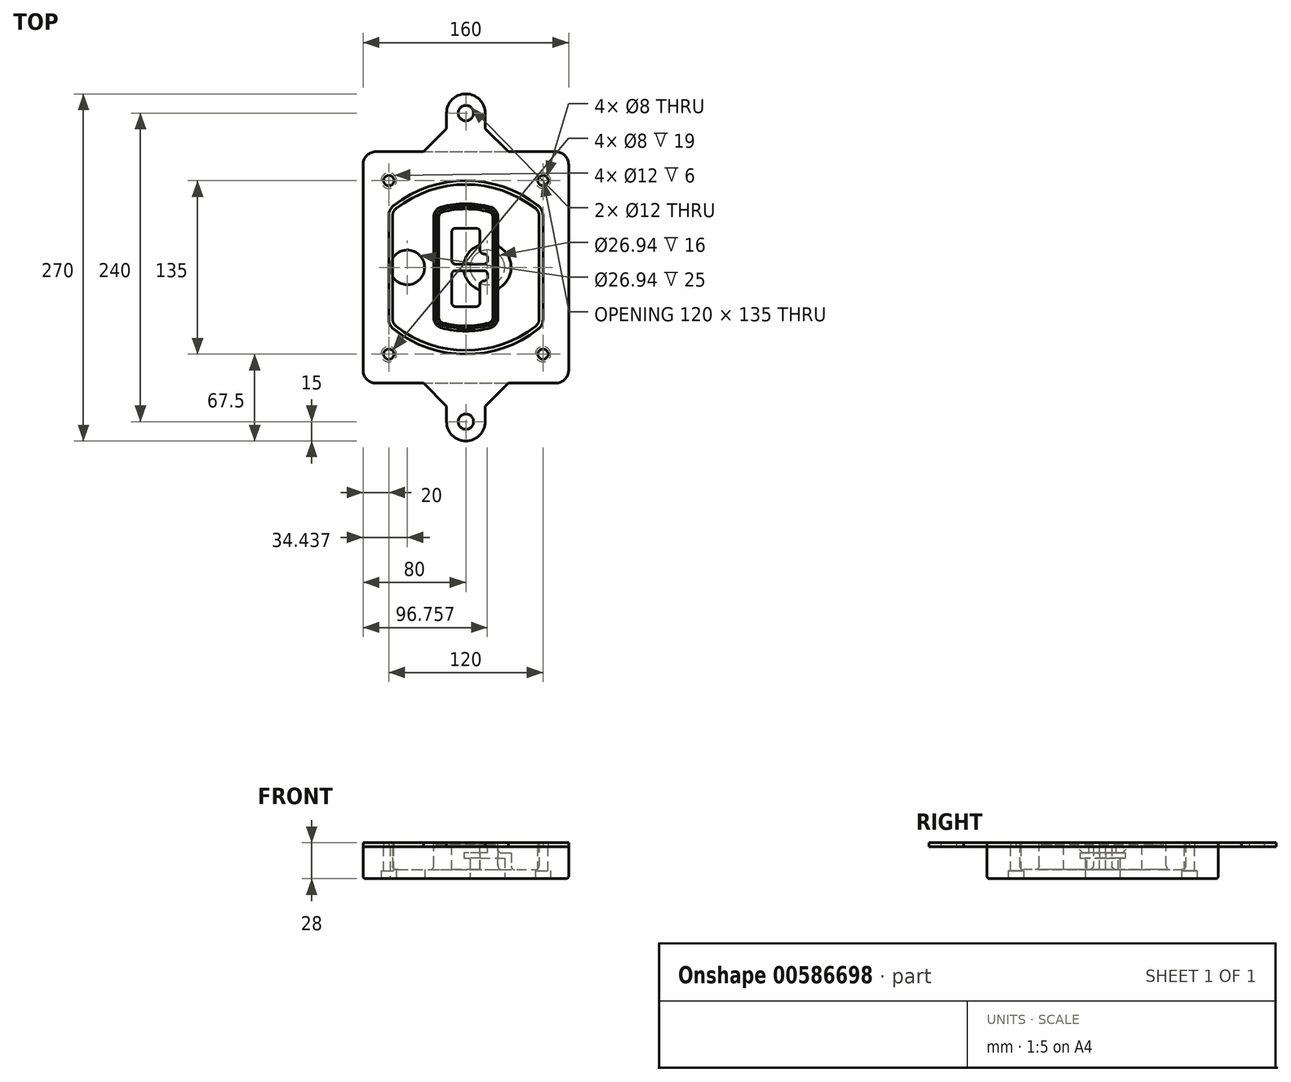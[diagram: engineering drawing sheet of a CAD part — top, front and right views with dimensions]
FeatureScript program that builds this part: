
annotation { "Feature Type Name" : "Feature", "Feature Type Description" : "" }
export const myFeature = defineFeature(function(context is Context, id is Id, definition is map)
    precondition{}
    {
        {
            var Q0;
            Q0=qCreatedBy(makeId("Top.planeOp"),FACE);
            var sketch = newSketch(context, id + "F0", { "sketchPlane" : qUnion([Q0])});
            skPoint(sketch, "E0.rect.middle", {"position": v(0, 0) * mm});
            skLineSegment(sketch, "E1.bottom", {"start": v(-70, -90) * mm, "end": v(70, -90) * mm});
            skLineSegment(sketch, "E1.top", {"start": v(-70, 90) * mm, "end": v(70, 90) * mm});
            skLineSegment(sketch, "E1.left", {"start": v(-80, -80) * mm, "end": v(-80, 80) * mm});
            skLineSegment(sketch, "E1.right", {"start": v(80, -80) * mm, "end": v(80, 80) * mm});
            skLineSegment(sketch, "E2", {"start": v(-80, 90) * mm, "end": v(80, -90) * mm, "construction": true});
            skLineSegment(sketch, "E3", {"start": v(80, 90) * mm, "end": v(-80, -90) * mm, "construction": true});
            skCircle(sketch, "E4", {"center": v(-60, 67.5) * mm, "radius": 4 * mm});
            skCircle(sketch, "E5", {"center": v(60, 67.5) * mm, "radius": 4 * mm});
            skCircle(sketch, "E6", {"center": v(60, -67.5) * mm, "radius": 4 * mm});
            skCircle(sketch, "E7", {"center": v(-60, -67.5) * mm, "radius": 4 * mm});
            skLineSegment(sketch, "E8", {"start": v(-60, 67.5) * mm, "end": v(60, 67.5) * mm, "construction": true});
            skLineSegment(sketch, "E9", {"start": v(60, 67.5) * mm, "end": v(60, -67.5) * mm, "construction": true});
            skLineSegment(sketch, "E10", {"start": v(60, -67.5) * mm, "end": v(-60, -67.5) * mm, "construction": true});
            skLineSegment(sketch, "E11", {"start": v(-60, -67.5) * mm, "end": v(-60, 67.5) * mm, "construction": true});
            skLineSegment(sketch, "E12", {"start": v(-60, 40.3) * mm, "end": v(-60, -40.3) * mm});
            skLineSegment(sketch, "E13", {"start": v(60, 40.3) * mm, "end": v(60, -40.3) * mm});
            skArc(sketch, "E14", {"start": v(56.15, 48.18) * mm, "mid": v(0, 67.5) * mm, "end": v(-56.15, 48.18) * mm});
            skArc(sketch, "E15", {"start": v(-56.15, -48.18) * mm, "mid": v(0, -67.5) * mm, "end": v(56.15, -48.18) * mm});
            skLineSegment(sketch, "E16", {"start": v(-60, 0) * mm, "end": v(60, 0) * mm, "construction": true});
            skPoint(sketch, "E17.visualSharp", {"position": v(-60, -45) * mm});
            skArc(sketch, "E17.filletArc", {"start": v(-60, -40.3) * mm, "mid": v(-58.99, -44.68) * mm, "end": v(-56.15, -48.18) * mm});
            skPoint(sketch, "E18.visualSharp", {"position": v(-60, 45) * mm});
            skArc(sketch, "E18.filletArc", {"start": v(-56.15, 48.18) * mm, "mid": v(-58.99, 44.68) * mm, "end": v(-60, 40.3) * mm});
            skPoint(sketch, "E19.visualSharp", {"position": v(60, 45) * mm});
            skArc(sketch, "E19.filletArc", {"start": v(60, 40.3) * mm, "mid": v(58.99, 44.68) * mm, "end": v(56.15, 48.18) * mm});
            skPoint(sketch, "E20.visualSharp", {"position": v(60, -45) * mm});
            skArc(sketch, "E20.filletArc", {"start": v(56.15, -48.18) * mm, "mid": v(58.99, -44.68) * mm, "end": v(60, -40.3) * mm});
            skPoint(sketch, "E21.visualSharp", {"position": v(-80, 90) * mm});
            skArc(sketch, "E21.filletArc", {"start": v(-70, 90) * mm, "mid": v(-77.07, 87.07) * mm, "end": v(-80, 80) * mm});
            skPoint(sketch, "E22.visualSharp", {"position": v(80, 90) * mm});
            skArc(sketch, "E22.filletArc", {"start": v(80, 80) * mm, "mid": v(77.07, 87.07) * mm, "end": v(70, 90) * mm});
            skPoint(sketch, "E23.visualSharp", {"position": v(80, -90) * mm});
            skArc(sketch, "E23.filletArc", {"start": v(70, -90) * mm, "mid": v(77.07, -87.07) * mm, "end": v(80, -80) * mm});
            skPoint(sketch, "E24.visualSharp", {"position": v(-80, -90) * mm});
            skArc(sketch, "E24.filletArc", {"start": v(-80, -80) * mm, "mid": v(-77.07, -87.07) * mm, "end": v(-70, -90) * mm});
            skArc(sketch, "E25.0", {"start": v(57, 40.3) * mm, "mid": v(56.3, 43.36) * mm, "end": v(54.3, 45.81) * mm});
            skLineSegment(sketch, "E25.1", {"start": v(57, 40.3) * mm, "end": v(57, -40.3) * mm});
            skArc(sketch, "E25.2", {"start": v(54.3, -45.81) * mm, "mid": v(56.3, -43.36) * mm, "end": v(57, -40.3) * mm});
            skArc(sketch, "E25.3", {"start": v(-54.3, -45.81) * mm, "mid": v(0, -64.5) * mm, "end": v(54.3, -45.81) * mm});
            skArc(sketch, "E25.4", {"start": v(-57, -40.3) * mm, "mid": v(-56.3, -43.36) * mm, "end": v(-54.3, -45.81) * mm});
            skArc(sketch, "E25.5", {"start": v(54.3, 45.81) * mm, "mid": v(0, 64.5) * mm, "end": v(-54.3, 45.81) * mm});
            skLineSegment(sketch, "E25.6", {"start": v(-57, 40.3) * mm, "end": v(-57, -40.3) * mm});
            skArc(sketch, "E25.7", {"start": v(-54.3, 45.81) * mm, "mid": v(-56.3, 43.36) * mm, "end": v(-57, 40.3) * mm});
            skArc(sketch, "E26.0", {"start": v(-58.62, 51.33) * mm, "mid": v(-62.58, 46.43) * mm, "end": v(-64, 40.3) * mm});
            skArc(sketch, "E26.1", {"start": v(58.62, 51.33) * mm, "mid": v(0, 71.5) * mm, "end": v(-58.62, 51.33) * mm});
            skArc(sketch, "E26.2", {"start": v(64, 40.3) * mm, "mid": v(62.58, 46.43) * mm, "end": v(58.62, 51.33) * mm});
            skLineSegment(sketch, "E26.3", {"start": v(64, 40.3) * mm, "end": v(64, -40.3) * mm});
            skArc(sketch, "E26.4", {"start": v(58.62, -51.33) * mm, "mid": v(62.58, -46.43) * mm, "end": v(64, -40.3) * mm});
            skLineSegment(sketch, "E26.5", {"start": v(-64, 40.3) * mm, "end": v(-64, -40.3) * mm});
            skArc(sketch, "E26.6", {"start": v(-58.62, -51.33) * mm, "mid": v(0, -71.5) * mm, "end": v(58.62, -51.33) * mm});
            skArc(sketch, "E26.7", {"start": v(-64, -40.3) * mm, "mid": v(-62.58, -46.43) * mm, "end": v(-58.62, -51.33) * mm});
            skSolve(sketch);
        }
        {
            var Q0;
            Q0=makeQuery(id+"F0.imprint","IMPRINT",FACE,{"disambiguationData":[TD([[makeQuery(id+"F0.imprint","IMPRINT",EDGE,{"derivedFrom":sQuery(id+"F0.wireOp",EDGE,"E1.bottom")}),1.0]])]});
            var Q1;
            Q1=makeQuery(id+"F0.imprint","IMPRINT",FACE,{"disambiguationData":[TD([[makeQuery(id+"F0.imprint","IMPRINT",EDGE,{"derivedFrom":sQuery(id+"F0.wireOp",EDGE,"E12")}),1.0]])]});
            var Q2;
            Q2=makeQuery(id+"F0.imprint","IMPRINT",FACE,{"disambiguationData":[TD([[makeQuery(id+"F0.imprint","IMPRINT",EDGE,{"derivedFrom":sQuery(id+"F0.wireOp",EDGE,"E25.0")}),1.0]])]});
            var Q3;
            Q3=makeQuery(id+"F0.imprint","IMPRINT",FACE,{"disambiguationData":[TD([[makeQuery(id+"F0.imprint","IMPRINT",EDGE,{"derivedFrom":sQuery(id+"F0.wireOp",EDGE,"E12")}),-1.0]])]});
            extrude(context, id + "F1", {"entities" : qUnion([Q0, Q1, Q2, Q3]), "oppositeDirection" : true, "depth" : 25 * mm});
        }
        {
            var Q0;
            Q0=makeQuery(id+"F0.imprint","IMPRINT",FACE,{"disambiguationData":[TD([[makeQuery(id+"F0.imprint","IMPRINT",EDGE,{"derivedFrom":sQuery(id+"F0.wireOp",EDGE,"E12")}),1.0]])]});
            extrude(context, id + "F2", {"entities" : qUnion([Q0]), "operationType" : NewBodyOperationType.ADD, "depth" : 3 * mm});
        }
        {
            var Q0;
            Q0=makeQuery(id+"F0.imprint","IMPRINT",FACE,{"disambiguationData":[TD([[makeQuery(id+"F0.imprint","IMPRINT",EDGE,{"derivedFrom":sQuery(id+"F0.wireOp",EDGE,"E25.0")}),1.0]])]});
            extrude(context, id + "F3", {"entities" : qUnion([Q0]), "operationType" : NewBodyOperationType.REMOVE, "oppositeDirection" : true, "depth" : 18 * mm});
        }
        {
            var Q0;
            Q0=makeQuery(id+"F2.opExtrude","CAP_FACE",FACE,{"disambiguationData":[OSD([sQuery(id+"F0.wireOp",EDGE,"E12"),sQuery(id+"F0.wireOp",EDGE,"E13"),sQuery(id+"F0.wireOp",EDGE,"E14"),sQuery(id+"F0.wireOp",EDGE,"E15"),sQuery(id+"F0.wireOp",EDGE,"E17.filletArc"),sQuery(id+"F0.wireOp",EDGE,"E18.filletArc"),sQuery(id+"F0.wireOp",EDGE,"E19.filletArc"),sQuery(id+"F0.wireOp",EDGE,"E20.filletArc"),sQuery(id+"F0.wireOp",EDGE,"E25.0"),sQuery(id+"F0.wireOp",EDGE,"E25.1"),sQuery(id+"F0.wireOp",EDGE,"E25.2"),sQuery(id+"F0.wireOp",EDGE,"E25.3"),sQuery(id+"F0.wireOp",EDGE,"E25.4"),sQuery(id+"F0.wireOp",EDGE,"E25.5"),sQuery(id+"F0.wireOp",EDGE,"E25.6"),sQuery(id+"F0.wireOp",EDGE,"E25.7")])],"isStart":false});
            var sketch = newSketch(context, id + "F4", { "sketchPlane" : qUnion([Q0])});
            skArc(sketch, "E27.0", {"start": v(-19.08, -46.97) * mm, "mid": v(0, -49.5) * mm, "end": v(19.08, -46.97) * mm});
            skArc(sketch, "E28.0", {"start": v(19.08, 46.97) * mm, "mid": v(0, 49.5) * mm, "end": v(-19.08, 46.97) * mm});
            skLineSegment(sketch, "E29", {"start": v(-25, 39.25) * mm, "end": v(-25, -39.25) * mm});
            skLineSegment(sketch, "E30", {"start": v(25, 39.25) * mm, "end": v(25, -39.25) * mm});
            skLineSegment(sketch, "E31", {"start": v(-25, 45.1) * mm, "end": v(25, 45.1) * mm, "construction": true});
            skLineSegment(sketch, "E32", {"start": v(-25, -45.1) * mm, "end": v(25, -45.1) * mm, "construction": true});
            skPoint(sketch, "E33.visualSharp", {"position": v(-25, 45.1) * mm});
            skArc(sketch, "E33.filletArc", {"start": v(-19.08, 46.97) * mm, "mid": v(-23.35, 44.11) * mm, "end": v(-25, 39.25) * mm});
            skPoint(sketch, "E34.visualSharp", {"position": v(25, 45.1) * mm});
            skArc(sketch, "E34.filletArc", {"start": v(25, 39.25) * mm, "mid": v(23.35, 44.11) * mm, "end": v(19.08, 46.97) * mm});
            skPoint(sketch, "E35.visualSharp", {"position": v(25, -45.1) * mm});
            skArc(sketch, "E35.filletArc", {"start": v(19.08, -46.97) * mm, "mid": v(23.35, -44.11) * mm, "end": v(25, -39.25) * mm});
            skPoint(sketch, "E36.visualSharp", {"position": v(-25, -45.1) * mm});
            skArc(sketch, "E36.filletArc", {"start": v(-25, -39.25) * mm, "mid": v(-23.35, -44.11) * mm, "end": v(-19.08, -46.97) * mm});
            skArc(sketch, "E37.0", {"start": v(54.3, 45.81) * mm, "mid": v(0, 64.5) * mm, "end": v(-54.3, 45.81) * mm});
            skArc(sketch, "E37.1", {"start": v(-54.3, 45.81) * mm, "mid": v(-56.3, 43.36) * mm, "end": v(-57, 40.3) * mm});
            skLineSegment(sketch, "E37.2", {"start": v(-57, 40.3) * mm, "end": v(-57, -40.3) * mm});
            skArc(sketch, "E37.3", {"start": v(-57, -40.3) * mm, "mid": v(-56.3, -43.36) * mm, "end": v(-54.3, -45.81) * mm});
            skArc(sketch, "E37.4", {"start": v(-54.3, -45.81) * mm, "mid": v(0, -64.5) * mm, "end": v(54.3, -45.81) * mm});
            skArc(sketch, "E37.5", {"start": v(54.3, -45.81) * mm, "mid": v(56.3, -43.36) * mm, "end": v(57, -40.3) * mm});
            skLineSegment(sketch, "E37.6", {"start": v(57, 40.3) * mm, "end": v(57, -40.3) * mm});
            skArc(sketch, "E37.7", {"start": v(57, 40.3) * mm, "mid": v(56.3, 43.36) * mm, "end": v(54.3, 45.81) * mm});
            skLineSegment(sketch, "E38.0", {"start": v(23, 39.25) * mm, "end": v(23, -39.25) * mm});
            skArc(sketch, "E38.1", {"start": v(18.56, -45.04) * mm, "mid": v(21.76, -42.9) * mm, "end": v(23, -39.25) * mm});
            skArc(sketch, "E38.2", {"start": v(-18.56, -45.04) * mm, "mid": v(0, -47.5) * mm, "end": v(18.56, -45.04) * mm});
            skArc(sketch, "E38.3", {"start": v(-23, -39.25) * mm, "mid": v(-21.76, -42.9) * mm, "end": v(-18.56, -45.04) * mm});
            skLineSegment(sketch, "E38.4", {"start": v(-23, 39.25) * mm, "end": v(-23, -39.25) * mm});
            skArc(sketch, "E38.5", {"start": v(23, 39.25) * mm, "mid": v(21.76, 42.9) * mm, "end": v(18.56, 45.04) * mm});
            skArc(sketch, "E38.6", {"start": v(-18.56, 45.04) * mm, "mid": v(-21.76, 42.9) * mm, "end": v(-23, 39.25) * mm});
            skArc(sketch, "E38.7", {"start": v(18.56, 45.04) * mm, "mid": v(0, 47.5) * mm, "end": v(-18.56, 45.04) * mm});
            skArc(sketch, "E39.0", {"start": v(21, 39.25) * mm, "mid": v(20.18, 41.68) * mm, "end": v(18.04, 43.1) * mm});
            skLineSegment(sketch, "E39.1", {"start": v(21, 39.25) * mm, "end": v(21, -39.25) * mm});
            skArc(sketch, "E39.2", {"start": v(18.04, -43.1) * mm, "mid": v(20.18, -41.68) * mm, "end": v(21, -39.25) * mm});
            skArc(sketch, "E39.3", {"start": v(-18.04, -43.1) * mm, "mid": v(0, -45.5) * mm, "end": v(18.04, -43.1) * mm});
            skArc(sketch, "E39.4", {"start": v(-21, -39.25) * mm, "mid": v(-20.18, -41.68) * mm, "end": v(-18.04, -43.1) * mm});
            skArc(sketch, "E39.5", {"start": v(18.04, 43.1) * mm, "mid": v(0, 45.5) * mm, "end": v(-18.04, 43.1) * mm});
            skLineSegment(sketch, "E39.6", {"start": v(-21, 39.25) * mm, "end": v(-21, -39.25) * mm});
            skArc(sketch, "E39.7", {"start": v(-18.04, 43.1) * mm, "mid": v(-20.18, 41.68) * mm, "end": v(-21, 39.25) * mm});
            skLineSegment(sketch, "E40", {"start": v(-25, 0) * mm, "end": v(25, 0) * mm, "construction": true});
            skLineSegment(sketch, "E41", {"start": v(-11, 5.5) * mm, "end": v(-11, 27.5) * mm});
            skLineSegment(sketch, "E42", {"start": v(-8, 30.5) * mm, "end": v(8, 30.5) * mm});
            skLineSegment(sketch, "E43", {"start": v(11, 27.5) * mm, "end": v(11, 13.5) * mm});
            skLineSegment(sketch, "E44", {"start": v(14, 10.5) * mm, "end": v(14, 10.5) * mm});
            skLineSegment(sketch, "E45", {"start": v(17, 7.5) * mm, "end": v(17, 5.5) * mm});
            skLineSegment(sketch, "E46", {"start": v(14, 2.5) * mm, "end": v(-8, 2.5) * mm});
            skPoint(sketch, "E47.visualSharp", {"position": v(-11, 30.5) * mm});
            skArc(sketch, "E47.filletArc", {"start": v(-8, 30.5) * mm, "mid": v(-10.12, 29.62) * mm, "end": v(-11, 27.5) * mm});
            skPoint(sketch, "E48.visualSharp", {"position": v(11, 30.5) * mm});
            skArc(sketch, "E48.filletArc", {"start": v(11, 27.5) * mm, "mid": v(10.12, 29.62) * mm, "end": v(8, 30.5) * mm});
            skPoint(sketch, "E49.visualSharp", {"position": v(11, 10.5) * mm});
            skArc(sketch, "E49.filletArc", {"start": v(11, 13.5) * mm, "mid": v(11.88, 11.38) * mm, "end": v(14, 10.5) * mm});
            skPoint(sketch, "E50.visualSharp", {"position": v(17, 10.5) * mm});
            skArc(sketch, "E50.filletArc", {"start": v(17, 7.5) * mm, "mid": v(16.12, 9.62) * mm, "end": v(14, 10.5) * mm});
            skPoint(sketch, "E51.visualSharp", {"position": v(17, 2.5) * mm});
            skArc(sketch, "E51.filletArc", {"start": v(14, 2.5) * mm, "mid": v(16.12, 3.38) * mm, "end": v(17, 5.5) * mm});
            skPoint(sketch, "E52.visualSharp", {"position": v(-11, 2.5) * mm});
            skArc(sketch, "E52.filletArc", {"start": v(-11, 5.5) * mm, "mid": v(-10.12, 3.38) * mm, "end": v(-8, 2.5) * mm});
            skLineSegment(sketch, "E53.0.MirrorCS", {"start": v(14, -2.5) * mm, "end": v(-8, -2.5) * mm});
            skArc(sketch, "E54.0.MirrorCS", {"start": v(-11, -5.5) * mm, "mid": v(-10.12, -3.38) * mm, "end": v(-8, -2.5) * mm});
            skLineSegment(sketch, "E55.0.MirrorCS", {"start": v(-11, -5.5) * mm, "end": v(-11, -27.5) * mm});
            skArc(sketch, "E56.0.MirrorCS", {"start": v(-8, -30.5) * mm, "mid": v(-10.12, -29.62) * mm, "end": v(-11, -27.5) * mm});
            skLineSegment(sketch, "E57.0.MirrorCS", {"start": v(-8, -30.5) * mm, "end": v(8, -30.5) * mm});
            skArc(sketch, "E58.0.MirrorCS", {"start": v(11, -27.5) * mm, "mid": v(10.12, -29.62) * mm, "end": v(8, -30.5) * mm});
            skLineSegment(sketch, "E59.0.MirrorCS", {"start": v(11, -27.5) * mm, "end": v(11, -13.5) * mm});
            skArc(sketch, "E60.0.MirrorCS", {"start": v(11, -13.5) * mm, "mid": v(11.88, -11.38) * mm, "end": v(14, -10.5) * mm});
            skArc(sketch, "E61.0.MirrorCS", {"start": v(17, -7.5) * mm, "mid": v(16.12, -9.62) * mm, "end": v(14, -10.5) * mm});
            skLineSegment(sketch, "E62.0.MirrorCS", {"start": v(17, -7.5) * mm, "end": v(17, -5.5) * mm});
            skArc(sketch, "E63.0.MirrorCS", {"start": v(14, -2.5) * mm, "mid": v(16.12, -3.38) * mm, "end": v(17, -5.5) * mm});
            skSolve(sketch);
        }
        {
            var Q0;
            Q0=makeQuery(id+"F4.imprint","IMPRINT",FACE,{"disambiguationData":[TD([[makeQuery(id+"F4.imprint","IMPRINT",EDGE,{"derivedFrom":sQuery(id+"F4.wireOp",EDGE,"E27.0")}),1.0]])]});
            var Q1;
            Q1=makeQuery(id+"F4.imprint","IMPRINT",FACE,{"disambiguationData":[TD([[makeQuery(id+"F4.imprint","IMPRINT",EDGE,{"derivedFrom":sQuery(id+"F4.wireOp",EDGE,"E38.0")}),-1.0]])]});
            var Q2;
            Q2=makeQuery(id+"F4.imprint","IMPRINT",FACE,{"disambiguationData":[TD([[makeQuery(id+"F4.imprint","IMPRINT",EDGE,{"derivedFrom":sQuery(id+"F4.wireOp",EDGE,"E39.0")}),1.0]])]});
            extrude(context, id + "F5", {"entities" : qUnion([Q0, Q1, Q2]), "operationType" : NewBodyOperationType.ADD, "endBound" : BoundingType.UP_TO_NEXT, "oppositeDirection" : true, "depth" : 25 * mm});
        }
        {
            var Q0;
            Q0=makeQuery(id+"F4.imprint","IMPRINT",FACE,{"disambiguationData":[TD([[makeQuery(id+"F4.imprint","IMPRINT",EDGE,{"derivedFrom":sQuery(id+"F4.wireOp",EDGE,"E38.0")}),-1.0]])]});
            extrude(context, id + "F6", {"entities" : qUnion([Q0]), "operationType" : NewBodyOperationType.REMOVE, "oppositeDirection" : true, "depth" : 2 * mm});
        }
        {
            var Q0;
            Q0=makeQuery(id+"F1.opExtrude","CAP_FACE",FACE,{"disambiguationData":[OSD([sQuery(id+"F0.wireOp",EDGE,"E1.bottom"),sQuery(id+"F0.wireOp",EDGE,"E1.top"),sQuery(id+"F0.wireOp",EDGE,"E1.left"),sQuery(id+"F0.wireOp",EDGE,"E1.right"),sQuery(id+"F0.wireOp",EDGE,"E4"),sQuery(id+"F0.wireOp",EDGE,"E5"),sQuery(id+"F0.wireOp",EDGE,"E6"),sQuery(id+"F0.wireOp",EDGE,"E7"),sQuery(id+"F0.wireOp",EDGE,"E21.filletArc"),sQuery(id+"F0.wireOp",EDGE,"E22.filletArc"),sQuery(id+"F0.wireOp",EDGE,"E23.filletArc"),sQuery(id+"F0.wireOp",EDGE,"E24.filletArc")])],"isStart":false});
            var sketch = newSketch(context, id + "F7", { "sketchPlane" : qUnion([Q0])});
            skCircle(sketch, "E64", {"center": v(16.76, 0) * mm, "radius": 13.47 * mm});
            skCircle(sketch, "E65", {"center": v(-45.56, 0) * mm, "radius": 13.47 * mm});
            skLineSegment(sketch, "E66", {"start": v(80, 0) * mm, "end": v(-80, 0) * mm});
            skCircle(sketch, "E67", {"center": v(16.76, 0) * mm, "radius": 18.47 * mm});
            skCircle(sketch, "E68", {"center": v(60, -67.5) * mm, "radius": 6 * mm});
            skCircle(sketch, "E69", {"center": v(-60, -67.5) * mm, "radius": 6 * mm});
            skCircle(sketch, "E70", {"center": v(-60, 67.5) * mm, "radius": 6 * mm});
            skCircle(sketch, "E71", {"center": v(60, 67.5) * mm, "radius": 6 * mm});
            skSolve(sketch);
        }
        {
            var Q0;
            {var subQ1=sQuery(id+"F7.wireOp",EDGE,"E66");var subQ4=sQuery(id+"F7.wireOp",EDGE,"E64");var subQ6=makeQuery(id+"F7.imprint","INTERSECT",VERTEX,{"disambiguationData":[OD(0.0)],"derivedFrom":[subQ4,subQ1]});Q0=makeQuery(id+"F7.imprint","IMPRINT",FACE,{"disambiguationData":[TD([[makeQuery(id+"F7.imprint","IMPRINT",EDGE,{"disambiguationData":[TD([[subQ6,-1.0]])],"derivedFrom":subQ4}),-1.0]])]});}
            var Q1;
            {var subQ0=sQuery(id+"F7.wireOp",EDGE,"E66");var subQ1=sQuery(id+"F7.wireOp",EDGE,"E64");var subQ3=makeQuery(id+"F7.imprint","INTERSECT",VERTEX,{"disambiguationData":[OD(0.0)],"derivedFrom":[subQ1,subQ0]});Q1=makeQuery(id+"F7.imprint","IMPRINT",FACE,{"disambiguationData":[TD([[makeQuery(id+"F7.imprint","IMPRINT",EDGE,{"disambiguationData":[TD([[subQ3,-1.0]])],"derivedFrom":subQ1}),1.0]])]});}
            var Q2;
            {var subQ0=sQuery(id+"F7.wireOp",EDGE,"E66");var subQ1=sQuery(id+"F7.wireOp",EDGE,"E64");var subQ3=makeQuery(id+"F7.imprint","INTERSECT",VERTEX,{"disambiguationData":[OD(0.0)],"derivedFrom":[subQ1,subQ0]});Q2=makeQuery(id+"F7.imprint","IMPRINT",FACE,{"disambiguationData":[TD([[makeQuery(id+"F7.imprint","IMPRINT",EDGE,{"disambiguationData":[TD([[subQ3,1.0]])],"derivedFrom":subQ1}),1.0]])]});}
            var Q3;
            {var subQ1=sQuery(id+"F7.wireOp",EDGE,"E66");var subQ4=sQuery(id+"F7.wireOp",EDGE,"E64");var subQ6=makeQuery(id+"F7.imprint","INTERSECT",VERTEX,{"disambiguationData":[OD(0.0)],"derivedFrom":[subQ4,subQ1]});Q3=makeQuery(id+"F7.imprint","IMPRINT",FACE,{"disambiguationData":[TD([[makeQuery(id+"F7.imprint","IMPRINT",EDGE,{"disambiguationData":[TD([[subQ6,1.0]])],"derivedFrom":subQ4}),-1.0]])]});}
            extrude(context, id + "F8", {"entities" : qUnion([Q0, Q1, Q2, Q3]), "operationType" : NewBodyOperationType.ADD, "oppositeDirection" : true, "depth" : 20 * mm});
        }
        {
            var Q0;
            {var subQ0=sQuery(id+"F7.wireOp",EDGE,"E66");var subQ1=sQuery(id+"F7.wireOp",EDGE,"E64");var subQ3=makeQuery(id+"F7.imprint","INTERSECT",VERTEX,{"disambiguationData":[OD(0.0)],"derivedFrom":[subQ1,subQ0]});Q0=makeQuery(id+"F7.imprint","IMPRINT",FACE,{"disambiguationData":[TD([[makeQuery(id+"F7.imprint","IMPRINT",EDGE,{"disambiguationData":[TD([[subQ3,-1.0]])],"derivedFrom":subQ1}),1.0]])]});}
            var Q1;
            {var subQ0=sQuery(id+"F7.wireOp",EDGE,"E66");var subQ1=sQuery(id+"F7.wireOp",EDGE,"E64");var subQ3=makeQuery(id+"F7.imprint","INTERSECT",VERTEX,{"disambiguationData":[OD(0.0)],"derivedFrom":[subQ1,subQ0]});Q1=makeQuery(id+"F7.imprint","IMPRINT",FACE,{"disambiguationData":[TD([[makeQuery(id+"F7.imprint","IMPRINT",EDGE,{"disambiguationData":[TD([[subQ3,1.0]])],"derivedFrom":subQ1}),1.0]])]});}
            extrude(context, id + "F9", {"entities" : qUnion([Q0, Q1]), "operationType" : NewBodyOperationType.REMOVE, "oppositeDirection" : true, "depth" : 16 * mm});
        }
        {
            var Q0;
            {var subQ0=sQuery(id+"F7.wireOp",EDGE,"E66");var subQ1=sQuery(id+"F7.wireOp",EDGE,"E65");var subQ3=makeQuery(id+"F7.imprint","INTERSECT",VERTEX,{"disambiguationData":[OD(0.0)],"derivedFrom":[subQ1,subQ0]});Q0=makeQuery(id+"F7.imprint","IMPRINT",FACE,{"disambiguationData":[TD([[makeQuery(id+"F7.imprint","IMPRINT",EDGE,{"disambiguationData":[TD([[subQ3,-1.0]])],"derivedFrom":subQ1}),1.0]])]});}
            var Q1;
            {var subQ0=sQuery(id+"F7.wireOp",EDGE,"E66");var subQ1=sQuery(id+"F7.wireOp",EDGE,"E65");var subQ3=makeQuery(id+"F7.imprint","INTERSECT",VERTEX,{"disambiguationData":[OD(0.0)],"derivedFrom":[subQ1,subQ0]});Q1=makeQuery(id+"F7.imprint","IMPRINT",FACE,{"disambiguationData":[TD([[makeQuery(id+"F7.imprint","IMPRINT",EDGE,{"disambiguationData":[TD([[subQ3,1.0]])],"derivedFrom":subQ1}),1.0]])]});}
            extrude(context, id + "F10", {"entities" : qUnion([Q0, Q1]), "operationType" : NewBodyOperationType.REMOVE, "oppositeDirection" : true, "depth" : 25 * mm});
        }
        {
            var Q0;
            Q0=makeQuery(id+"F7.imprint","IMPRINT",FACE,{"disambiguationData":[TD([[makeQuery(id+"F7.imprint","IMPRINT",EDGE,{"derivedFrom":sQuery(id+"F7.wireOp",EDGE,"E68")}),1.0]])]});
            var Q1;
            Q1=makeQuery(id+"F7.imprint","IMPRINT",FACE,{"disambiguationData":[TD([[makeQuery(id+"F7.imprint","IMPRINT",EDGE,{"derivedFrom":makeQuery(id+"F1.opExtrude","CAP_EDGE",EDGE,{"disambiguationData":[OSD([sQuery(id+"F0.wireOp",EDGE,"E5")])],"isStart":false})}),-1.0]])]});
            var Q2;
            Q2=makeQuery(id+"F7.imprint","IMPRINT",FACE,{"disambiguationData":[TD([[makeQuery(id+"F7.imprint","IMPRINT",EDGE,{"derivedFrom":sQuery(id+"F7.wireOp",EDGE,"E69")}),1.0]])]});
            var Q3;
            Q3=makeQuery(id+"F7.imprint","IMPRINT",FACE,{"disambiguationData":[TD([[makeQuery(id+"F7.imprint","IMPRINT",EDGE,{"derivedFrom":makeQuery(id+"F1.opExtrude","CAP_EDGE",EDGE,{"disambiguationData":[OSD([sQuery(id+"F0.wireOp",EDGE,"E4")])],"isStart":false})}),-1.0]])]});
            var Q4;
            Q4=makeQuery(id+"F7.imprint","IMPRINT",FACE,{"disambiguationData":[TD([[makeQuery(id+"F7.imprint","IMPRINT",EDGE,{"derivedFrom":sQuery(id+"F7.wireOp",EDGE,"E70")}),1.0]])]});
            var Q5;
            Q5=makeQuery(id+"F7.imprint","IMPRINT",FACE,{"disambiguationData":[TD([[makeQuery(id+"F7.imprint","IMPRINT",EDGE,{"derivedFrom":makeQuery(id+"F1.opExtrude","CAP_EDGE",EDGE,{"disambiguationData":[OSD([sQuery(id+"F0.wireOp",EDGE,"E7")])],"isStart":false})}),-1.0]])]});
            var Q6;
            Q6=makeQuery(id+"F7.imprint","IMPRINT",FACE,{"disambiguationData":[TD([[makeQuery(id+"F7.imprint","IMPRINT",EDGE,{"derivedFrom":sQuery(id+"F7.wireOp",EDGE,"E71")}),1.0]])]});
            var Q7;
            Q7=makeQuery(id+"F7.imprint","IMPRINT",FACE,{"disambiguationData":[TD([[makeQuery(id+"F7.imprint","IMPRINT",EDGE,{"derivedFrom":makeQuery(id+"F1.opExtrude","CAP_EDGE",EDGE,{"disambiguationData":[OSD([sQuery(id+"F0.wireOp",EDGE,"E6")])],"isStart":false})}),-1.0]])]});
            extrude(context, id + "F11", {"entities" : qUnion([Q0, Q1, Q2, Q3, Q4, Q5, Q6, Q7]), "operationType" : NewBodyOperationType.REMOVE, "oppositeDirection" : true, "depth" : 6 * mm});
        }
        {
            var Q0;
            Q0=makeQuery(id+"F9.boolean.opBoolean","COPY",FACE,{"derivedFrom":makeQuery(id+"F9.opExtrude","CAP_FACE",FACE,{"disambiguationData":[OSD([sQuery(id+"F7.wireOp",EDGE,"E64")])],"isStart":false})});
            var sketch = newSketch(context, id + "F12", { "sketchPlane" : qUnion([Q0])});
            skArc(sketch, "E72.0", {"start": v(11, 17.55) * mm, "mid": v(2.57, 11.82) * mm, "end": v(-1.54, 2.5) * mm});
            skArc(sketch, "E72.1", {"start": v(-1.54, -2.5) * mm, "mid": v(2.57, -11.82) * mm, "end": v(11, -17.55) * mm});
            skLineSegment(sketch, "E73", {"start": v(-1.54, -2.5) * mm, "end": v(14, -2.5) * mm});
            skLineSegment(sketch, "E74.0", {"start": v(14, 2.5) * mm, "end": v(-1.54, 2.5) * mm});
            skArc(sketch, "E74.1", {"start": v(14, 2.5) * mm, "mid": v(16.12, 3.38) * mm, "end": v(17, 5.5) * mm});
            skLineSegment(sketch, "E74.2", {"start": v(17, 7.5) * mm, "end": v(17, 5.5) * mm});
            skArc(sketch, "E74.3", {"start": v(17, 7.5) * mm, "mid": v(16.12, 9.62) * mm, "end": v(14, 10.5) * mm});
            skArc(sketch, "E74.4", {"start": v(11, 13.5) * mm, "mid": v(11.88, 11.38) * mm, "end": v(14, 10.5) * mm});
            skLineSegment(sketch, "E74.5", {"start": v(11, 17.55) * mm, "end": v(11, 13.5) * mm});
            skLineSegment(sketch, "E74.7", {"start": v(14, -2.5) * mm, "end": v(-1.54, -2.5) * mm});
            skArc(sketch, "E74.8", {"start": v(14, -2.5) * mm, "mid": v(16.12, -3.38) * mm, "end": v(17, -5.5) * mm});
            skLineSegment(sketch, "E74.9", {"start": v(17, -7.5) * mm, "end": v(17, -5.5) * mm});
            skArc(sketch, "E74.10", {"start": v(17, -7.5) * mm, "mid": v(16.12, -9.62) * mm, "end": v(14, -10.5) * mm});
            skArc(sketch, "E74.11", {"start": v(11, -13.5) * mm, "mid": v(11.88, -11.38) * mm, "end": v(14, -10.5) * mm});
            skLineSegment(sketch, "E74.12", {"start": v(11, -17.55) * mm, "end": v(11, -13.5) * mm});
            skPoint(sketch, "E75.orphan", {"position": v(11, -27.5) * mm});
            skPoint(sketch, "E76.orphan", {"position": v(-8, -2.5) * mm});
            skPoint(sketch, "E77.orphan", {"position": v(-8, 2.5) * mm});
            skPoint(sketch, "E78.orphan", {"position": v(11, 27.5) * mm});
            skSolve(sketch);
        }
        {
            var Q0;
            {var subQ7=sQuery(id+"F12.wireOp",EDGE,"E72.0");var subQ14=sQuery(id+"F12.wireOp",EDGE,"E72.1");var subQ16=sQuery(id+"F12.wireOp",EDGE,"E74.1");var subQ18=sQuery(id+"F12.wireOp",EDGE,"E74.8");Q0=qUnion([makeQuery(id+"F12.imprint","IMPRINT",FACE,{"disambiguationData":[TD([[makeQuery(id+"F12.imprint","IMPRINT",EDGE,{"derivedFrom":subQ7}),1.0]])]}),makeQuery(id+"F12.imprint","IMPRINT",FACE,{"disambiguationData":[TD([[makeQuery(id+"F12.imprint","IMPRINT",EDGE,{"derivedFrom":subQ14}),1.0]])]}),makeQuery(id+"F12.imprint","IMPRINT",FACE,{"disambiguationData":[TD([[makeQuery(id+"F12.imprint","IMPRINT",EDGE,{"derivedFrom":subQ16}),1.0]])]}),makeQuery(id+"F12.imprint","IMPRINT",FACE,{"disambiguationData":[TD([[makeQuery(id+"F12.imprint","IMPRINT",EDGE,{"derivedFrom":subQ18}),-1.0]])]})]);}
            var Q1;
            Q1=makeQuery(id+"F5.boolean.opBoolean","SPLIT",FACE,{"disambiguationData":[TD([makeQuery(id+"F5.opExtrude","SWEPT_FACE",FACE,{"disambiguationData":[OSD([sQuery(id+"F4.wireOp",EDGE,"E41")])]})])],"derivedFrom":makeQuery(id+"F3.boolean.opBoolean","COPY",FACE,{"derivedFrom":makeQuery(id+"F3.opExtrude","CAP_FACE",FACE,{"disambiguationData":[OSD([sQuery(id+"F0.wireOp",EDGE,"E25.0"),sQuery(id+"F0.wireOp",EDGE,"E25.1"),sQuery(id+"F0.wireOp",EDGE,"E25.2"),sQuery(id+"F0.wireOp",EDGE,"E25.3"),sQuery(id+"F0.wireOp",EDGE,"E25.4"),sQuery(id+"F0.wireOp",EDGE,"E25.5"),sQuery(id+"F0.wireOp",EDGE,"E25.6"),sQuery(id+"F0.wireOp",EDGE,"E25.7")])],"isStart":false})})});
            extrude(context, id + "F13", {"entities" : qUnion([Q0]), "operationType" : NewBodyOperationType.REMOVE, "endBound" : BoundingType.UP_TO_SURFACE, "endBoundEntityFace" : qUnion([Q1]), "depth" : 25 * mm});
        }
        {
            var Q0;
            Q0=makeQuery(id+"F3.boolean.opBoolean","COPY",EDGE,{"derivedFrom":makeQuery(id+"F3.opExtrude","CAP_EDGE",EDGE,{"disambiguationData":[OSD([sQuery(id+"F0.wireOp",EDGE,"E25.6")])],"isStart":false})});
            var Q1;
            Q1=makeQuery(id+"F8.boolean.opBoolean","INTERSECT",EDGE,{"derivedFrom":[makeQuery(id+"F5.opExtrude","SWEPT_FACE",FACE,{"disambiguationData":[OSD([sQuery(id+"F4.wireOp",EDGE,"E30")])]}),makeQuery(id+"F8.opExtrude","CAP_FACE",FACE,{"disambiguationData":[OSD([sQuery(id+"F7.wireOp",EDGE,"E67")])],"isStart":false})]});
            var Q2;
            Q2=makeQuery(id+"F8.boolean.opBoolean","INTERSECT",EDGE,{"disambiguationData":[OD(1.0)],"derivedFrom":[makeQuery(id+"F5.opExtrude","SWEPT_FACE",FACE,{"disambiguationData":[OSD([sQuery(id+"F4.wireOp",EDGE,"E30")])]}),makeQuery(id+"F8.opExtrude","SWEPT_FACE",FACE,{"disambiguationData":[OSD([sQuery(id+"F7.wireOp",EDGE,"E67")])]})]});
            var Q3;
            {var subQ0=sQuery(id+"F4.wireOp",EDGE,"E30");Q3=makeQuery(id+"F8.boolean.opBoolean","SPLIT",EDGE,{"disambiguationData":[TD([makeQuery(id+"F5.opExtrude","SWEPT_FACE",FACE,{"disambiguationData":[OSD([sQuery(id+"F4.wireOp",EDGE,"E35.filletArc")])]})])],"derivedFrom":makeQuery(id+"F5.opExtrude","CAP_EDGE",EDGE,{"disambiguationData":[OSD([subQ0])],"isStart":false})});}
            var Q4;
            {var subQ0=sQuery(id+"F0.wireOp",EDGE,"E25.7");var subQ1=sQuery(id+"F0.wireOp",EDGE,"E25.1");var subQ2=sQuery(id+"F0.wireOp",EDGE,"E25.6");var subQ3=sQuery(id+"F0.wireOp",EDGE,"E25.5");var subQ4=sQuery(id+"F0.wireOp",EDGE,"E25.4");var subQ5=sQuery(id+"F0.wireOp",EDGE,"E25.0");var subQ6=sQuery(id+"F0.wireOp",EDGE,"E25.2");var subQ7=sQuery(id+"F0.wireOp",EDGE,"E25.3");Q4=makeQuery(id+"F8.boolean.opBoolean","INTERSECT",EDGE,{"derivedFrom":[makeQuery(id+"F5.boolean.opBoolean","SPLIT",FACE,{"disambiguationData":[TD([makeQuery(id+"F2.opExtrude","SWEPT_FACE",FACE,{"disambiguationData":[OSD([subQ5])]})])],"derivedFrom":makeQuery(id+"F3.boolean.opBoolean","COPY",FACE,{"derivedFrom":makeQuery(id+"F3.opExtrude","CAP_FACE",FACE,{"disambiguationData":[OSD([subQ5,subQ1,subQ6,subQ7,subQ4,subQ3,subQ2,subQ0])],"isStart":false})})}),makeQuery(id+"F8.opExtrude","SWEPT_FACE",FACE,{"disambiguationData":[OSD([sQuery(id+"F7.wireOp",EDGE,"E67")])]})]});}
            var Q5;
            Q5=makeQuery(id+"F8.boolean.opBoolean","INTERSECT",EDGE,{"disambiguationData":[OD(0.0)],"derivedFrom":[makeQuery(id+"F5.opExtrude","SWEPT_FACE",FACE,{"disambiguationData":[OSD([sQuery(id+"F4.wireOp",EDGE,"E30")])]}),makeQuery(id+"F8.opExtrude","SWEPT_FACE",FACE,{"disambiguationData":[OSD([sQuery(id+"F7.wireOp",EDGE,"E67")])]})]});
            fillet(context, id + "F14", {"entities" : qUnion([Q0, Q1, Q2, Q3, Q4, Q5]), "radius" : 3 * mm, "tangentPropagation" : true, "allowEdgeOverflow" : false});
        }
        {
            var Q0;
            Q0=makeQuery(id+"F1.opExtrude","CAP_EDGE",EDGE,{"disambiguationData":[OSD([sQuery(id+"F0.wireOp",EDGE,"E1.bottom")])],"isStart":false});
            fillet(context, id + "F15", {"entities" : qUnion([Q0]), "radius" : 2 * mm, "tangentPropagation" : true, "allowEdgeOverflow" : false});
        }
        {
            var Q0;
            {var subQ0=sQuery(id+"F0.wireOp",EDGE,"E21.filletArc");var subQ1=sQuery(id+"F0.wireOp",EDGE,"E7");var subQ2=sQuery(id+"F0.wireOp",EDGE,"E6");var subQ3=sQuery(id+"F0.wireOp",EDGE,"E5");var subQ4=sQuery(id+"F0.wireOp",EDGE,"E4");var subQ5=sQuery(id+"F0.wireOp",EDGE,"E22.filletArc");var subQ6=sQuery(id+"F0.wireOp",EDGE,"E1.bottom");var subQ7=sQuery(id+"F0.wireOp",EDGE,"E1.right");var subQ8=sQuery(id+"F0.wireOp",EDGE,"E1.top");var subQ9=sQuery(id+"F0.wireOp",EDGE,"E1.left");var subQ10=sQuery(id+"F0.wireOp",EDGE,"E23.filletArc");var subQ11=sQuery(id+"F0.wireOp",EDGE,"E24.filletArc");Q0=makeQuery(id+"F2.boolean.opBoolean","SPLIT",FACE,{"disambiguationData":[TD([makeQuery(id+"F1.opExtrude","SWEPT_FACE",FACE,{"disambiguationData":[OSD([subQ6])]})])],"derivedFrom":makeQuery(id+"F1.opExtrude","CAP_FACE",FACE,{"disambiguationData":[OSD([subQ6,subQ8,subQ9,subQ7,subQ4,subQ3,subQ2,subQ1,subQ0,subQ5,subQ10,subQ11])],"isStart":true})});}
            var sketch = newSketch(context, id + "F16", { "sketchPlane" : qUnion([Q0])});
            skLineSegment(sketch, "E79", {"start": v(0, 90) * mm, "end": v(0, 120) * mm, "construction": true});
            skCircle(sketch, "E80", {"center": v(0, 120) * mm, "radius": 6 * mm});
            skArc(sketch, "E81", {"start": v(15, 120) * mm, "mid": v(0, 135) * mm, "end": v(-15, 120) * mm});
            skLineSegment(sketch, "E82", {"start": v(-15, 120) * mm, "end": v(-15, 108) * mm});
            skLineSegment(sketch, "E83", {"start": v(-15, 108) * mm, "end": v(-33, 90) * mm});
            skLineSegment(sketch, "E84", {"start": v(15, 120) * mm, "end": v(15, 108) * mm});
            skLineSegment(sketch, "E85", {"start": v(15, 108) * mm, "end": v(33, 90) * mm});
            skLineSegment(sketch, "E86", {"start": v(-80, 0) * mm, "end": v(80, 0) * mm, "construction": true});
            skArc(sketch, "E87.MirrorCS", {"start": v(-15, 120) * mm, "mid": v(0, 135) * mm, "end": v(15, 120) * mm});
            skLineSegment(sketch, "E88.MirrorCS", {"start": v(15, -120) * mm, "end": v(15, -108) * mm});
            skLineSegment(sketch, "E89.MirrorCS", {"start": v(15, -108) * mm, "end": v(33, -90) * mm});
            skCircle(sketch, "E90.MirrorC", {"center": v(0, -120) * mm, "radius": 6 * mm});
            skLineSegment(sketch, "E91.MirrorCS", {"start": v(-15, -108) * mm, "end": v(-33, -90) * mm});
            skArc(sketch, "E92.MirrorCS", {"start": v(15, -120) * mm, "mid": v(0, -135) * mm, "end": v(-15, -120) * mm});
            skLineSegment(sketch, "E93.MirrorCS", {"start": v(-15, -120) * mm, "end": v(-15, -108) * mm});
            skArc(sketch, "E94.MirrorCS", {"start": v(-15, -120) * mm, "mid": v(0, -135) * mm, "end": v(15, -120) * mm});
            skLineSegment(sketch, "E95.MirrorCS", {"start": v(0, -90) * mm, "end": v(0, -120) * mm, "construction": true});
            skSolve(sketch);
        }
        {
            var Q0;
            Q0=makeQuery(id+"F16.imprint","IMPRINT",FACE,{"disambiguationData":[TD([[makeQuery(id+"F16.imprint","IMPRINT",EDGE,{"derivedFrom":makeQuery(id+"F1.opExtrude","CAP_EDGE",EDGE,{"disambiguationData":[OSD([sQuery(id+"F0.wireOp",EDGE,"E1.left")])],"isStart":true})}),-1.0]])]});
            var Q1;
            {var subQ1=sQuery(id+"F16.wireOp",EDGE,"E89.MirrorCS");Q1=makeQuery(id+"F16.imprint","IMPRINT",FACE,{"disambiguationData":[TD([[makeQuery(id+"F16.imprint","IMPRINT",EDGE,{"derivedFrom":subQ1}),1.0]])]});}
            var Q2;
            {var subQ0=sQuery(id+"F16.wireOp",EDGE,"E85");Q2=makeQuery(id+"F16.imprint","IMPRINT",FACE,{"disambiguationData":[TD([[makeQuery(id+"F16.imprint","IMPRINT",EDGE,{"derivedFrom":subQ0}),-1.0]])]});}
            var Q3;
            Q3=makeQuery(id+"F2.opExtrude","CAP_FACE",FACE,{"disambiguationData":[OSD([sQuery(id+"F0.wireOp",EDGE,"E12"),sQuery(id+"F0.wireOp",EDGE,"E13"),sQuery(id+"F0.wireOp",EDGE,"E14"),sQuery(id+"F0.wireOp",EDGE,"E15"),sQuery(id+"F0.wireOp",EDGE,"E17.filletArc"),sQuery(id+"F0.wireOp",EDGE,"E18.filletArc"),sQuery(id+"F0.wireOp",EDGE,"E19.filletArc"),sQuery(id+"F0.wireOp",EDGE,"E20.filletArc"),sQuery(id+"F0.wireOp",EDGE,"E25.0"),sQuery(id+"F0.wireOp",EDGE,"E25.1"),sQuery(id+"F0.wireOp",EDGE,"E25.2"),sQuery(id+"F0.wireOp",EDGE,"E25.3"),sQuery(id+"F0.wireOp",EDGE,"E25.4"),sQuery(id+"F0.wireOp",EDGE,"E25.5"),sQuery(id+"F0.wireOp",EDGE,"E25.6"),sQuery(id+"F0.wireOp",EDGE,"E25.7")])],"isStart":false});
            extrude(context, id + "F17", {"entities" : qUnion([Q0, Q1, Q2]), "endBound" : BoundingType.UP_TO_SURFACE, "depth" : 25 * mm, "endBoundEntityFace" : qUnion([Q3]), "offsetDistance" : 25 * mm});
        }
    });
